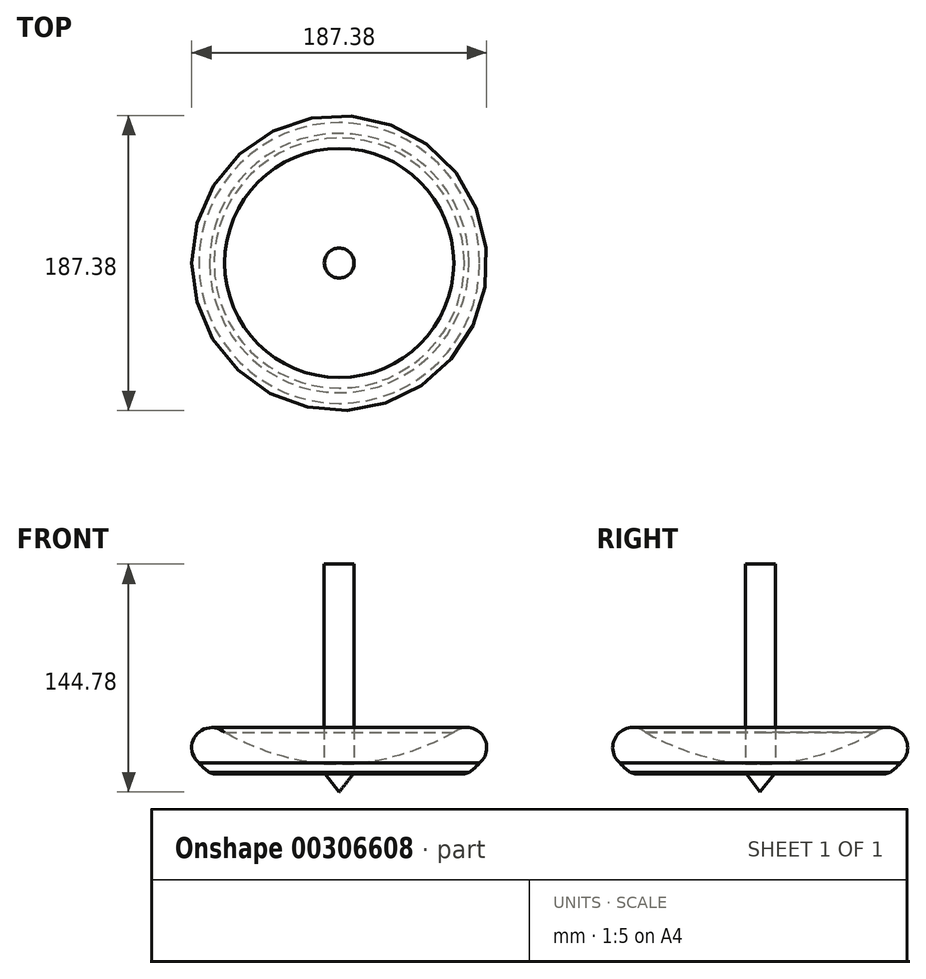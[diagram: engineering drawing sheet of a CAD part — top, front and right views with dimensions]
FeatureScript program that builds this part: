
annotation { "Feature Type Name" : "Feature", "Feature Type Description" : "" }
export const myFeature = defineFeature(function(context is Context, id is Id, definition is map)
    precondition{}
    {
        {
            var Q0;
            Q0=qCreatedBy(makeId("Front.planeOp"),FACE);
            var sketch = newSketch(context, id + "F0", { "sketchPlane" : qUnion([Q0])});
            skLineSegment(sketch, "E0", {"start": v(0, 0) * mm, "end": v(0, 9.44) * mm, "construction": true});
            skPoint(sketch, "E1.second.point", {"position": v(87.1, 14.42) * mm});
            skArc(sketch, "E2", {"start": v(9.53, 11.43) * mm, "mid": v(44.3, 18.86) * mm, "end": v(76.57, 33.79) * mm});
            skLineSegment(sketch, "E3", {"start": v(0, 5.08) * mm, "end": v(0, 0) * mm});
            skLineSegment(sketch, "E4", {"start": v(0, -6.35) * mm, "end": v(0, 0) * mm});
            skLineSegment(sketch, "E5.top", {"start": v(0, 138.43) * mm, "end": v(9.52, 138.43) * mm});
            skLineSegment(sketch, "E5.left", {"start": v(0, 5.08) * mm, "end": v(0, 138.43) * mm});
            skLineSegment(sketch, "E5.right", {"start": v(9.52, 11.43) * mm, "end": v(9.52, 138.43) * mm});
            skLineSegment(sketch, "E6", {"start": v(81, 21.88) * mm, "end": v(81, 9.18) * mm, "construction": true});
            skLineSegment(sketch, "E7", {"start": v(8.9, 5.08) * mm, "end": v(81, 5.08) * mm});
            skArc(sketch, "E8", {"start": v(81, 5.08) * mm, "mid": v(87.55, 10.4) * mm, "end": v(92.74, 17.06) * mm});
            skLineSegment(sketch, "E9", {"start": v(0, -6.35) * mm, "end": v(8.9, 5.08) * mm});
            skLineSegment(sketch, "E10", {"start": v(8.9, 5.08) * mm, "end": v(0, 5.08) * mm});
            skCircle(sketch, "E11", {"center": v(81, 21.88) * mm, "radius": 12.7 * mm});
            skSolve(sketch);
        }
        {
            var Q0;
            Q0 = qSketchRegion(id + "F0", true);
            var Q1;
            Q1=sQuery(id+"F0.wireOp",EDGE,"E0");
            revolve(context, id + "F1", {"entities" : qUnion([Q0]), "axis" : qUnion([Q1]), "revolveType" : RevolveType.FULL});
        }
        {
            var Q0;
            Q0=makeQuery(id+"F1.opRevolve","SWEPT_EDGE",EDGE,{"disambiguationData":[OSD([sQuery(id+"F0.wireOp",EDGE,"E7"),sQuery(id+"F0.wireOp",EDGE,"E8")])]});
            chamfer(context, id + "F2", {"entities" : qUnion([Q0]), "width" : 5.08 * mm, "tangentPropagation" : true});
        }
    });
